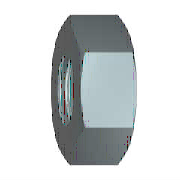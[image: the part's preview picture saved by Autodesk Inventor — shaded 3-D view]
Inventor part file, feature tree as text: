
AUTODESK INVENTOR PART (.ipt)
format: ipt  version: 2013 (Build 170138000, 138)  size: 171,008 bytes
history: native  units: mm (DEFAULTED — no unit token found)
features: sketch x3, chamfer x1, hole x1, other x1, plane x1
ambient origin geometry x7: Origin, YZ Plane, XZ Plane, X Axis, Y Axis, Z Axis, Center Point
bodies: Solid1 (feature_tree), Body (feature_tree)
feature tree (7):
  chamfer  "Chamfer1"  Distance=4.363323mm
  hole  "Thread"  [1 undecoded]
  other  "Work Axis1"
  plane  "Work Plane1"
  sketch  "Sketch1"  dims[d0=9.237604mm]
  sketch  "Sketch2"  dims[d1=4.7mm]
  sketch  "Sketch3"  dims[d2=0.0mm d3=4.363323mm d4=4.363323mm d5=8.0mm d6=8.0mm d7=90.0deg d25=4.134mm d26=6.0mm d27=4.0mm d28=2.0mm d29=14.3117mm d30=8.0mm d31=20.594885mm d8=0.433013mm d9=30.0deg d10=0.433013mm d11=30.0deg d13=0.0mm d14=0.0mm d39=0.0mm d40=0.433013mm d41=0.433013mm d42=0.0mm]
note: 1 required parameter value undecoded (feature->parameter linkage not recoverable at this tier; creation-order binding heuristic only, values carry confidence <= 0.55)
